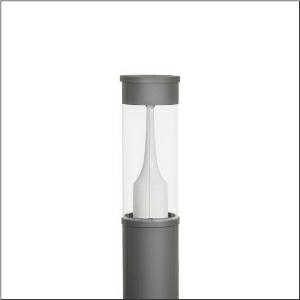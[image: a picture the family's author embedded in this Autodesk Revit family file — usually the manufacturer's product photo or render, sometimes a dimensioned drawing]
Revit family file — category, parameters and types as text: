
# Revit family: city-light_120_iq___pl1_2s_5xa5285rf14h_2286
name_source: partatom
category: Lighting Fixtures
units: mm (PartAtom-declared; Revit-internal decimal feet)

## family parameters
Cut with Voids When Loaded = No
Host = Face
Light Source = No
Part Type = Normal
Room Calculation Point = No
Round Connector Dimension = Use Diameter
Shared = No

## types (1)
- --- (1 x LED, 2970 lm, 18.5 W, 4000K)
    Apparent Load = 19 VA
    CIE Flux Codes = 23 62 94 96 100
    Color Rendering = 70
    Color Temperature = 4000K
    Default Elevation = 1800 mm
    Description = City-Light 120 iQ, bollard luminaire, Module 540 iQ-SR, primary light control with 3 zone facetted reflector, of plastic, silver coated, highly specular, structured, primary optical cover: cover, of PMMA, transparent, partly coated, light distribution: PL1.2s, primary light characteristic: symmetric, LED, High Power LED, rated luminous flux: 2.970lm, luminous efficacy: 161lm/W, light colour: 740, colour temperature: 4000K, control gear: iQ Street-Remote, control: pre-setting: logarithmic dimming characteristic, Street-Remote, Auto-Match, Temp-Guard, Lumen-Switch, Night-Set, Smart-Wire, Light-Fading, Desk-Remote (wireless, voltage-free reading and setting of iQ features in the workshop via application-optimized NFC function/RFID function), optimised constant luminous flux control (CLO 2.0), with terminal, 6-pole, max. 2.5mm², mains connection: 230..240V, AC, 50/60Hz, start of lifetime: 19W, end of service life: 20W, reduction: 9W, luminaire housing, cylindrical, of extruded aluminium section, coated, Siteco® metallic grey (DB 702S), length: 1.200mm, diameter: 200mm, Module 540 iQ-SR, traffic white (RAL 9016), equipment: standard, protection rating (complete): IP54, insulation class (complete): insulation class II (safety insulation), certification: CE, ENEC, VDE, packaging unit: 1 piece

Light Distribution: PL1.2s
    Height = 500 mm
    Lamp = 1 x LED
    Lamp Light Flux = 2970 lm
    Lamp Power = 18.5 W
    Lamp count = 1
    Length = 200 mm  [stored 0.656168 ft]
    Luminous efficacy = 161 lm/W
    Manufacturer = Siteco
    ModVariant = No
    Model = 5XA5285RF14H
    Mounting Place = Floor
    Mounting Type = Freestanding
    Number of Poles = 1
    OnlyDefault = Yes
    Power Factor = 1
    Product Name = City-Light 120 iQ | PL1.2s
    Product group = bollard luminaire
    ProductGroupID = 1304
    Protection Class = Protection class II
    Protection Degree = IP 54
    RLX_Detail_Level = 1
    RLX_Emergency_Light_Flux = 0 lm
    RLX_Emergency_Type = 0
    RLX_Emergency_Type_DB = No
    RlxData = <blob elided: 22413 chars, md5=b5665202>
    Socket = socket
    Standby Power = 0 W
    System Light Flux = 2970 lm
    System Power = 19 W
    Type Comments = factory setting: luminous flux: 100 % | dim-lin: 254 | 385 mA
    Type Image = l_1006922.jpg
    URL = http://relux.com
    VarID = @adj_166637
    Voltage = 0 V
    Weight = 0.00 kg
    Width = 0 mm  [stored 0 ft]

note: [stored X ft] marks values corroborated as IEEE doubles in the binary element streams (Revit-internal decimal feet)

## geometry (parser evidence)
native form markers: Blend x4, Sweep x12
no freeform markers — native parametric forms only
